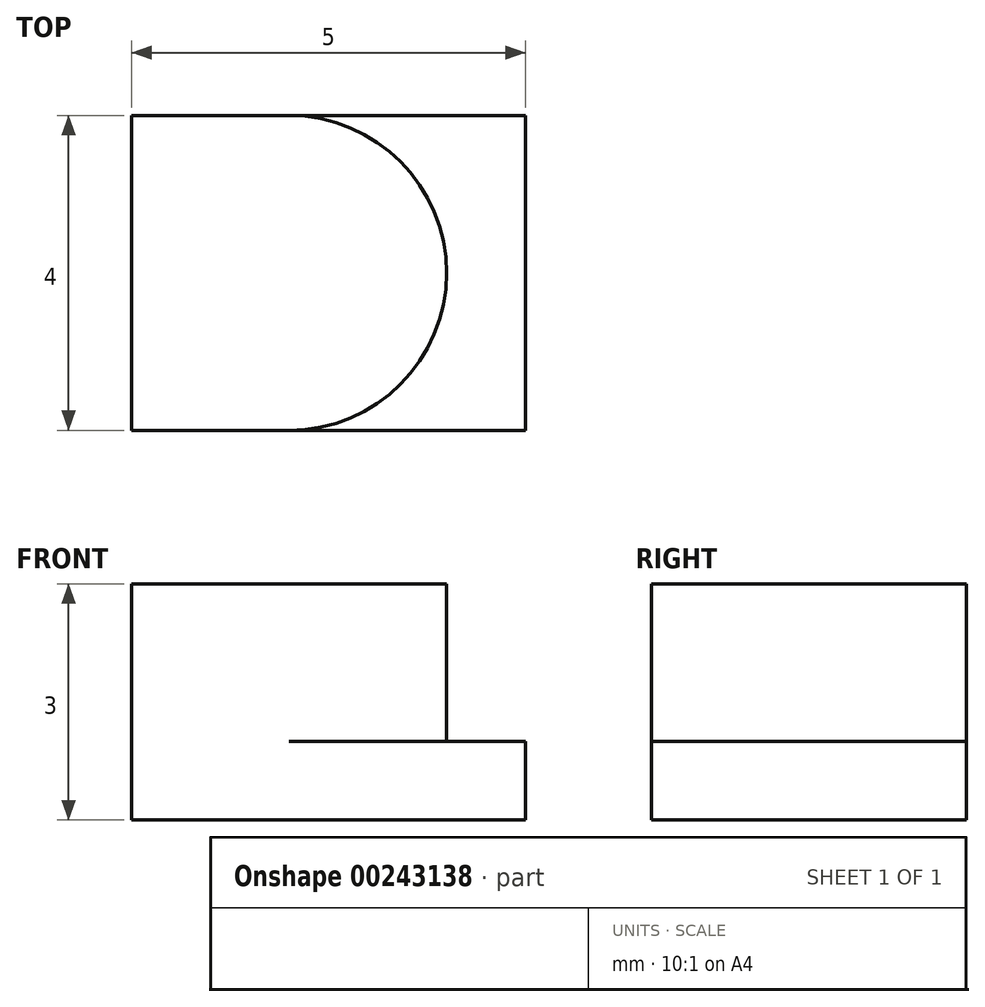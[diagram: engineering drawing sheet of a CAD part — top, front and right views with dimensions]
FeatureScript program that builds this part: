
annotation { "Feature Type Name" : "Feature", "Feature Type Description" : "" }
export const myFeature = defineFeature(function(context is Context, id is Id, definition is map)
    precondition{}
    {
        {
            var Q0;
            Q0=qCreatedBy(makeId("Front.planeOp"),FACE);
            var sketch = newSketch(context, id + "F0", { "sketchPlane" : qUnion([Q0])});
            skLineSegment(sketch, "E0", {"start": v(0, 0) * mm, "end": v(5, 0) * mm});
            skLineSegment(sketch, "E1", {"start": v(5, 0) * mm, "end": v(5, 1) * mm});
            skLineSegment(sketch, "E2", {"start": v(5, 1) * mm, "end": v(0, 1) * mm});
            skLineSegment(sketch, "E3", {"start": v(0, 1) * mm, "end": v(0, 0) * mm});
            skSolve(sketch);
        }
        {
            var Q0;
            Q0 = qSketchRegion(id + "F0", true);
            extrude(context, id + "F1", {"entities" : qUnion([Q0]), "depth" : 4 * mm});
        }
        {
            var Q0;
            Q0=makeQuery(id+"F1.opExtrude","SWEPT_FACE",FACE,{"disambiguationData":[OSD([sQuery(id+"F0.wireOp",EDGE,"E2")])]});
            var sketch = newSketch(context, id + "F2", { "sketchPlane" : qUnion([Q0])});
            skLineSegment(sketch, "E4", {"start": v(0, 0) * mm, "end": v(2, 0) * mm});
            skLineSegment(sketch, "E5", {"start": v(0, 0) * mm, "end": v(0, -4) * mm});
            skLineSegment(sketch, "E6", {"start": v(0, -4) * mm, "end": v(2, -4) * mm});
            skArc(sketch, "E7", {"start": v(2, -4) * mm, "mid": v(4, -2) * mm, "end": v(2, 0) * mm});
            skSolve(sketch);
        }
        {
            var Q0;
            Q0 = qSketchRegion(id + "F2", true);
            extrude(context, id + "F3", {"entities" : qUnion([Q0]), "operationType" : NewBodyOperationType.ADD, "depth" : 2 * mm});
        }
    });
